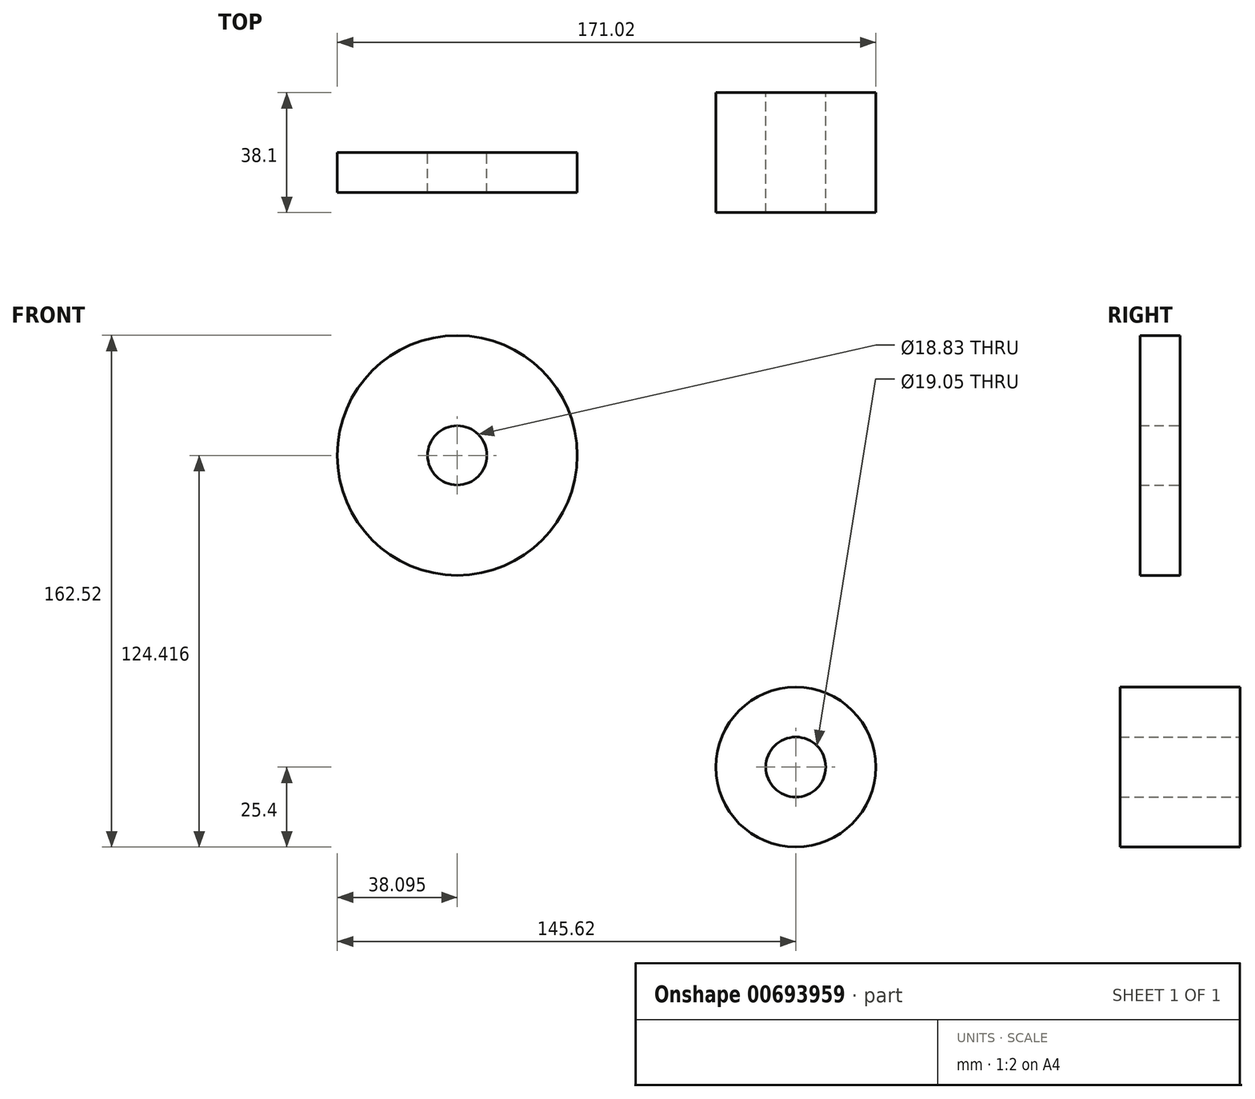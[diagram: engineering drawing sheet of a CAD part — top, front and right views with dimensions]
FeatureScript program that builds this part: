
annotation { "Feature Type Name" : "Feature", "Feature Type Description" : "" }
export const myFeature = defineFeature(function(context is Context, id is Id, definition is map)
    precondition{}
    {
        {
            var Q0;
            Q0=qCreatedBy(makeId("Front.planeOp"),FACE);
            var sketch = newSketch(context, id + "F0", { "sketchPlane" : qUnion([Q0])});
            skCircle(sketch, "E0", {"center": v(0, 0) * mm, "radius": 9.53 * mm});
            skCircle(sketch, "E1", {"center": v(0, 0) * mm, "radius": 25.4 * mm});
            skSolve(sketch);
        }
        {
            var Q0;
            Q0=makeQuery(id+"F0.imprint","IMPRINT",FACE,{"disambiguationData":[TD([[makeQuery(id+"F0.imprint","IMPRINT",EDGE,{"derivedFrom":sQuery(id+"F0.wireOp",EDGE,"E0")}),-1.0]])]});
            extrude(context, id + "F1", {"entities" : qUnion([Q0]), "depth" : 19.05 * mm, "offsetDistance" : 25.4 * mm});
        }
        {
            var Q0;
            Q0=makeQuery(id+"F1.opExtrude","SWEPT_BODY",BODY,{"disambiguationData":[OSD([sQuery(id+"F0.wireOp",EDGE,"E0"),sQuery(id+"F0.wireOp",EDGE,"E1")])]});
            var Q1;
            Q1=qCreatedBy(makeId("Front.planeOp"),FACE);
            mirror(context, id + "F2", {"operationType" : NewBodyOperationType.ADD, "entities" : qUnion([Q0]), "mirrorPlane" : qUnion([Q1])});
        }
        {
            var Q0;
            Q0=qCreatedBy(makeId("Front.planeOp"),FACE);
            var sketch = newSketch(context, id + "F3", { "sketchPlane" : qUnion([Q0])});
            skCircle(sketch, "E2", {"center": v(-107.52, 99.02) * mm, "radius": 38.1 * mm});
            skCircle(sketch, "E3", {"center": v(-107.52, 99.02) * mm, "radius": 9.42 * mm});
            skSolve(sketch);
        }
        {
            var Q0;
            Q0=makeQuery(id+"F3.imprint","IMPRINT",FACE,{"disambiguationData":[TD([[makeQuery(id+"F3.imprint","IMPRINT",EDGE,{"derivedFrom":sQuery(id+"F3.wireOp",EDGE,"E2")}),1.0]])]});
            extrude(context, id + "F4", {"entities" : qUnion([Q0]), "depth" : 12.7 * mm, "offsetDistance" : 25.4 * mm});
        }
    });
